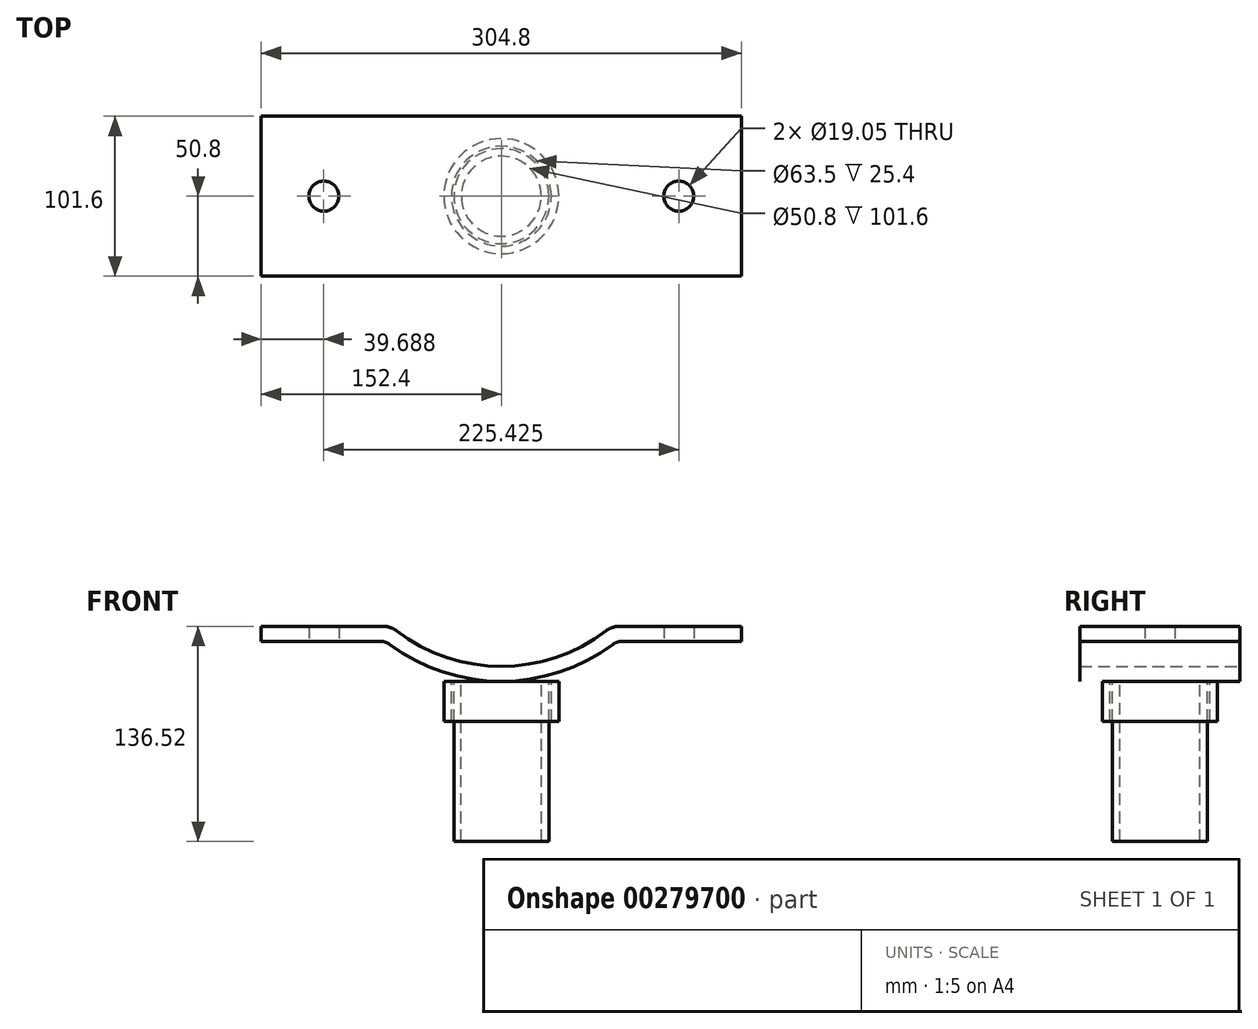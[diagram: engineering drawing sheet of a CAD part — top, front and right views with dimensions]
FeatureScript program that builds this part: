
annotation { "Feature Type Name" : "Feature", "Feature Type Description" : "" }
export const myFeature = defineFeature(function(context is Context, id is Id, definition is map)
    precondition{}
    {
        {
            var Q0;
            Q0=qCreatedBy(makeId("Top.planeOp"),FACE);
            var sketch = newSketch(context, id + "F0", { "sketchPlane" : qUnion([Q0])});
            skCircle(sketch, "E0", {"center": v(0, 0) * mm, "radius": 25.4 * mm});
            skCircle(sketch, "E1", {"center": v(0, 0) * mm, "radius": 30.16 * mm});
            skCircle(sketch, "E2", {"center": v(0, 0) * mm, "radius": 31.75 * mm});
            skCircle(sketch, "E3", {"center": v(0, 0) * mm, "radius": 36.51 * mm});
            skSolve(sketch);
        }
        {
            var Q0;
            Q0=makeQuery(id+"F0.imprint","IMPRINT",FACE,{"disambiguationData":[TD([[makeQuery(id+"F0.imprint","IMPRINT",EDGE,{"derivedFrom":sQuery(id+"F0.wireOp",EDGE,"E0")}),-1.0]])]});
            extrude(context, id + "F1", {"entities" : qUnion([Q0]), "oppositeDirection" : true, "depth" : 25.4 * mm});
        }
        {
            var Q0;
            Q0=makeQuery(id+"F0.imprint","IMPRINT",FACE,{"disambiguationData":[TD([[makeQuery(id+"F0.imprint","IMPRINT",EDGE,{"derivedFrom":sQuery(id+"F0.wireOp",EDGE,"E0")}),-1.0]])]});
            extrude(context, id + "F2", {"entities" : qUnion([Q0]), "operationType" : NewBodyOperationType.ADD, "oppositeDirection" : true, "depth" : 101.6 * mm});
        }
        {
            var Q0;
            Q0=makeQuery(id+"F0.imprint","IMPRINT",FACE,{"disambiguationData":[TD([[makeQuery(id+"F0.imprint","IMPRINT",EDGE,{"derivedFrom":sQuery(id+"F0.wireOp",EDGE,"E2")}),-1.0]])]});
            extrude(context, id + "F3", {"entities" : qUnion([Q0]), "oppositeDirection" : true, "depth" : 25.4 * mm});
        }
        {
            var Q0;
            Q0=qCreatedBy(makeId("Front.planeOp"),FACE);
            var sketch = newSketch(context, id + "F4", { "sketchPlane" : qUnion([Q0])});
            skPoint(sketch, "E4.first.point", {"position": v(0, 0) * mm});
            skArc(sketch, "E5", {"start": v(-70.14, 34.92) * mm, "mid": v(0, 9.52) * mm, "end": v(70.14, 34.92) * mm});
            skLineSegment(sketch, "E6", {"start": v(-152.4, 34.92) * mm, "end": v(-70.14, 34.92) * mm});
            skLineSegment(sketch, "E7", {"start": v(152.4, 25.4) * mm, "end": v(73.5, 25.4) * mm});
            skLineSegment(sketch, "E8", {"start": v(152.4, 34.92) * mm, "end": v(152.4, 25.4) * mm});
            skLineSegment(sketch, "E9", {"start": v(-152.4, 34.92) * mm, "end": v(-152.4, 25.4) * mm});
            skArc(sketch, "E10.trimOffspring", {"start": v(-73.5, 25.4) * mm, "mid": v(0, 0) * mm, "end": v(73.5, 25.4) * mm});
            skLineSegment(sketch, "E11.trimOffspring", {"start": v(70.14, 34.92) * mm, "end": v(152.4, 34.92) * mm});
            skLineSegment(sketch, "E12.trimOffspring", {"start": v(-73.5, 25.4) * mm, "end": v(-152.4, 25.4) * mm});
            skSolve(sketch);
        }
        {
            var Q0;
            Q0=makeQuery(id+"F4.imprint","IMPRINT",FACE,{"disambiguationData":[TD([[makeQuery(id+"F4.imprint","IMPRINT",EDGE,{"derivedFrom":sQuery(id+"F4.wireOp",EDGE,"E5")}),-1.0]])]});
            extrude(context, id + "F5", {"entities" : qUnion([Q0]), "endBound" : BoundingType.SYMMETRIC, "depth" : 101.6 * mm});
        }
        {
            var Q0;
            Q0=makeQuery(id+"F5.opExtrude","SWEPT_EDGE",EDGE,{"disambiguationData":[OSD([sQuery(id+"F4.wireOp",EDGE,"E5"),sQuery(id+"F4.wireOp",EDGE,"E11.trimOffspring")])]});
            var Q1;
            Q1=makeQuery(id+"F5.opExtrude","SWEPT_EDGE",EDGE,{"disambiguationData":[OSD([sQuery(id+"F4.wireOp",EDGE,"E5"),sQuery(id+"F4.wireOp",EDGE,"E6")])]});
            fillet(context, id + "F6", {"entities" : qUnion([Q0, Q1]), "radius" : 12.7 * mm, "tangentPropagation" : true, "allowEdgeOverflow" : false});
        }
        {
            var Q0;
            Q0=makeQuery(id+"F5.opExtrude","SWEPT_EDGE",EDGE,{"disambiguationData":[OSD([sQuery(id+"F4.wireOp",EDGE,"E10.trimOffspring"),sQuery(id+"F4.wireOp",EDGE,"E12.trimOffspring")])]});
            var Q1;
            Q1=makeQuery(id+"F5.opExtrude","SWEPT_EDGE",EDGE,{"disambiguationData":[OSD([sQuery(id+"F4.wireOp",EDGE,"E7"),sQuery(id+"F4.wireOp",EDGE,"E10.trimOffspring")])]});
            fillet(context, id + "F7", {"entities" : qUnion([Q0, Q1]), "radius" : 9.52 * mm, "tangentPropagation" : true, "allowEdgeOverflow" : false});
        }
        {
            var Q0;
            Q0=qCreatedBy(makeId("Top.planeOp"),FACE);
            var sketch = newSketch(context, id + "F8", { "sketchPlane" : qUnion([Q0])});
            skCircle(sketch, "E13", {"center": v(-112.71, 0) * mm, "radius": 9.53 * mm});
            skCircle(sketch, "E14", {"center": v(112.71, 0) * mm, "radius": 9.53 * mm});
            skSolve(sketch);
        }
        {
            var Q0;
            Q0=makeQuery(id+"F8.imprint","IMPRINT",FACE,{"disambiguationData":[TD([[makeQuery(id+"F8.imprint","IMPRINT",EDGE,{"derivedFrom":sQuery(id+"F8.wireOp",EDGE,"E13")}),1.0]])]});
            var Q1;
            Q1=makeQuery(id+"F8.imprint","IMPRINT",FACE,{"disambiguationData":[TD([[makeQuery(id+"F8.imprint","IMPRINT",EDGE,{"derivedFrom":sQuery(id+"F8.wireOp",EDGE,"E14")}),1.0]])]});
            var Q2;
            Q2=sQuery(id+"F8.wireOp",EDGE,"E13");
            var Q3;
            Q3=sQuery(id+"F8.wireOp",EDGE,"E14");
            extrude(context, id + "F9", {"entities" : qUnion([Q0, Q1]), "operationType" : NewBodyOperationType.REMOVE, "surfaceEntities" : qUnion([Q2, Q3]), "endBound" : BoundingType.THROUGH_ALL, "depth" : 25.4 * mm});
        }
    });
